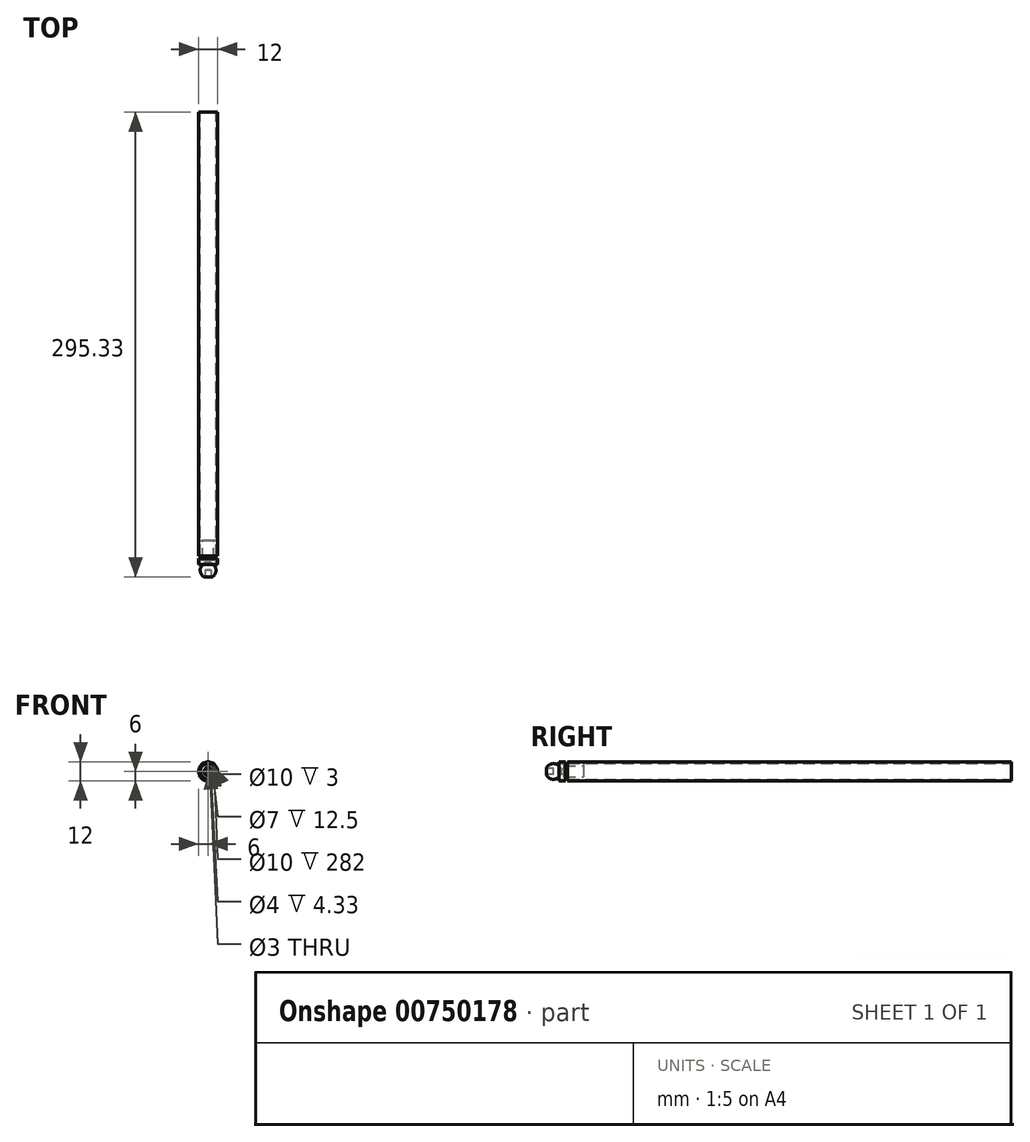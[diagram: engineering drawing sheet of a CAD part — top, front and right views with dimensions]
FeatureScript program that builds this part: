
annotation { "Feature Type Name" : "Feature", "Feature Type Description" : "" }
export const myFeature = defineFeature(function(context is Context, id is Id, definition is map)
    precondition{}
    {
        {
            var Q0;
            Q0=qCreatedBy(makeId("Top.planeOp"),FACE);
            var sketch = newSketch(context, id + "F0", { "sketchPlane" : qUnion([Q0])});
            skLineSegment(sketch, "E0", {"start": v(0, 0) * mm, "end": v(0, -6.5) * mm});
            skLineSegment(sketch, "E1", {"start": v(-5, 0) * mm, "end": v(-5, -3) * mm});
            skLineSegment(sketch, "E2", {"start": v(-5, -3) * mm, "end": v(-3.57, -3) * mm});
            skArc(sketch, "E3", {"start": v(-3.57, -3) * mm, "mid": v(-1.94, -1.9) * mm, "end": v(0, -1.5) * mm});
            skLineSegment(sketch, "E4", {"start": v(-1.5, 0) * mm, "end": v(-1.5, -1.73) * mm});
            skArc(sketch, "E5", {"start": v(-3.57, -3) * mm, "mid": v(-4.95, -7.18) * mm, "end": v(-2.5, -10.83) * mm});
            skArc(sketch, "E6", {"start": v(0, -11.5) * mm, "mid": v(4.6, -8.44) * mm, "end": v(3.57, -3) * mm, "construction": true});
            skLineSegment(sketch, "E7.bottom", {"start": v(-6, 286) * mm, "end": v(-5, 286) * mm});
            skLineSegment(sketch, "E8", {"start": v(-5, 0) * mm, "end": v(-1.5, 0) * mm});
            skLineSegment(sketch, "E9", {"start": v(0, -11.5) * mm, "end": v(0, -6.5) * mm, "construction": true});
            skLineSegment(sketch, "E10", {"start": v(0, -6.5) * mm, "end": v(-2, -6.5) * mm});
            skLineSegment(sketch, "E11", {"start": v(-2, -6.5) * mm, "end": v(-2, -10.83) * mm});
            skArc(sketch, "E12", {"start": v(-2, -11.08) * mm, "mid": v(-1.02, -11.4) * mm, "end": v(0, -11.5) * mm, "construction": true});
            skLineSegment(sketch, "E13", {"start": v(-2, -10.83) * mm, "end": v(-2.5, -10.83) * mm});
            skLineSegment(sketch, "E14", {"start": v(-2, -10.83) * mm, "end": v(-2, -11.08) * mm, "construction": true});
            skArc(sketch, "E15", {"start": v(-2.5, -10.83) * mm, "mid": v(-2.25, -10.96) * mm, "end": v(-2, -11.08) * mm, "construction": true});
            skSolve(sketch);
        }
        {
            var Q0;
            {var subQ3=sQuery(id+"F0.wireOp",EDGE,"E1");Q0=makeQuery(id+"F0.imprint","IMPRINT",FACE,{"disambiguationData":[TD([[makeQuery(id+"F0.imprint","IMPRINT",EDGE,{"derivedFrom":subQ3}),1.0]])]});}
            var Q1;
            Q1=sQuery(id+"F0.wireOp",EDGE,"E0");
            revolve(context, id + "F1", {"surfaceOperationType" : NewSurfaceOperationType.NEW, "entities" : qUnion([Q0]), "axis" : qUnion([Q1]), "revolveType" : RevolveType.FULL});
        }
        {
            var Q0;
            Q0=qCreatedBy(makeId("Top.planeOp"),FACE);
            var sketch = newSketch(context, id + "F2", { "sketchPlane" : qUnion([Q0])});
            skLineSegment(sketch, "E16.bottom", {"start": v(-6, 2.5) * mm, "end": v(-5, 2.5) * mm});
            skLineSegment(sketch, "E16.top", {"start": v(-6, 284.5) * mm, "end": v(-5, 284.5) * mm});
            skLineSegment(sketch, "E16.left", {"start": v(-6, 2.5) * mm, "end": v(-6, 284.5) * mm});
            skLineSegment(sketch, "E16.right", {"start": v(-5, 2.5) * mm, "end": v(-5, 284.5) * mm});
            skSolve(sketch);
        }
        {
            var Q0;
            Q0=makeQuery(id+"F2.imprint","IMPRINT",FACE,{"disambiguationData":[TD([[makeQuery(id+"F2.imprint","IMPRINT",EDGE,{"derivedFrom":sQuery(id+"F2.wireOp",EDGE,"E16.bottom")}),1.0]])]});
            var Q1;
            Q1=sQuery(id+"F0.wireOp",EDGE,"E0");
            revolve(context, id + "F3", {"surfaceOperationType" : NewSurfaceOperationType.NEW, "entities" : qUnion([Q0]), "axis" : qUnion([Q1]), "revolveType" : RevolveType.FULL});
        }
        {
            var Q0;
            Q0=qCreatedBy(makeId("Top.planeOp"),FACE);
            var sketch = newSketch(context, id + "F4", { "sketchPlane" : qUnion([Q0])});
            skLineSegment(sketch, "E17", {"start": v(-6, 1) * mm, "end": v(-6, -3) * mm});
            skLineSegment(sketch, "E18", {"start": v(-6, -3) * mm, "end": v(-5, -3) * mm});
            skLineSegment(sketch, "E19", {"start": v(-5, -3) * mm, "end": v(-5, 0) * mm});
            skLineSegment(sketch, "E20.0", {"start": v(-5, 2.5) * mm, "end": v(5, 2.5) * mm, "construction": true});
            skPoint(sketch, "E21", {"position": v(0, 2.5) * mm});
            skLineSegment(sketch, "E22", {"start": v(-6, 1) * mm, "end": v(-5, 1) * mm});
            skLineSegment(sketch, "E23", {"start": v(-5, 1) * mm, "end": v(-5, 2.5) * mm});
            skLineSegment(sketch, "E24", {"start": v(-5, 2.5) * mm, "end": v(-5, 12.5) * mm});
            skLineSegment(sketch, "E25", {"start": v(-5, 12.5) * mm, "end": v(-3.5, 12.5) * mm});
            skLineSegment(sketch, "E26", {"start": v(-3.5, 12.5) * mm, "end": v(-3.5, 0) * mm});
            skLineSegment(sketch, "E27", {"start": v(-5, 0) * mm, "end": v(-3.5, 0) * mm});
            skSolve(sketch);
        }
        {
            var Q0;
            Q0=makeQuery(id+"F4.imprint","IMPRINT",FACE,{"disambiguationData":[TD([[makeQuery(id+"F4.imprint","IMPRINT",EDGE,{"derivedFrom":sQuery(id+"F4.wireOp",EDGE,"E17")}),1.0]])]});
            var Q1;
            Q1=sQuery(id+"F0.wireOp",EDGE,"E0");
            revolve(context, id + "F5", {"surfaceOperationType" : NewSurfaceOperationType.NEW, "entities" : qUnion([Q0]), "axis" : qUnion([Q1]), "revolveType" : RevolveType.FULL});
        }
        {
            var Q0;
            {var subQ0=sQuery(id+"F0.wireOp",EDGE,"E5");Q0=makeQuery(id+"F0.imprint","IMPRINT",FACE,{"disambiguationData":[TD([[makeQuery(id+"F0.imprint","IMPRINT",EDGE,{"derivedFrom":subQ0}),1.0]])]});}
            var Q1;
            Q1=sQuery(id+"F0.wireOp",EDGE,"E9");
            revolve(context, id + "F6", {"surfaceOperationType" : NewSurfaceOperationType.NEW, "entities" : qUnion([Q0]), "axis" : qUnion([Q1]), "revolveType" : RevolveType.FULL});
        }
    });
